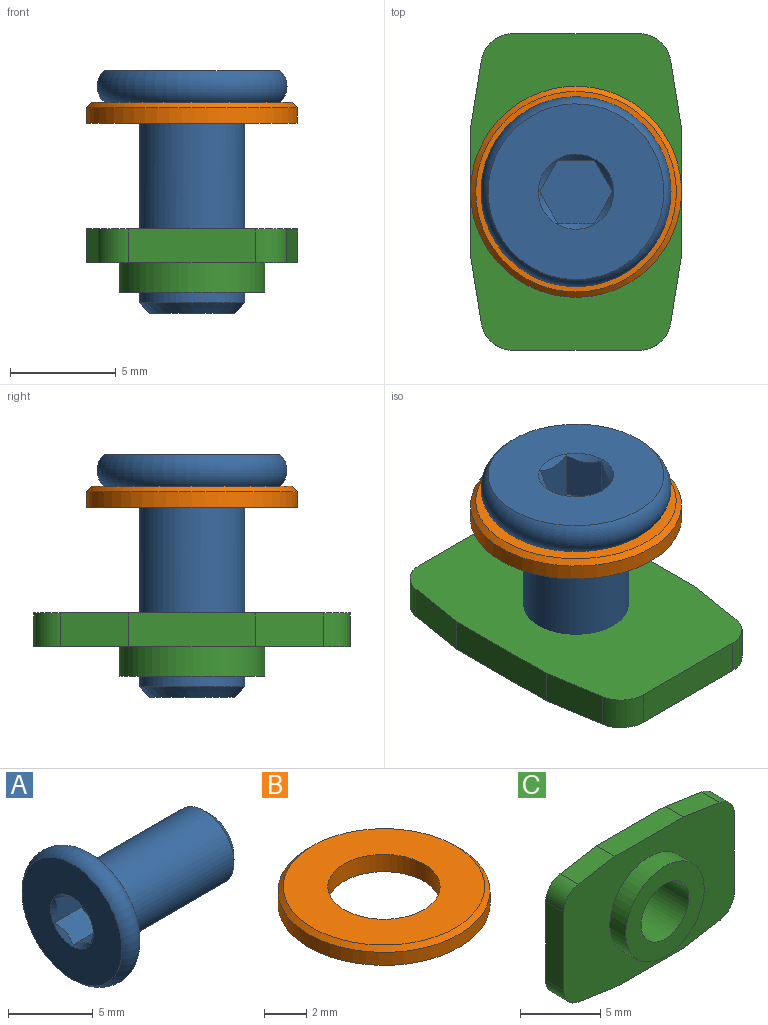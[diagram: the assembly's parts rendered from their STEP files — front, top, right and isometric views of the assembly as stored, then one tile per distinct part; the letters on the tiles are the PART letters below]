
ASSEMBLY  parts=3 mates=2
PART A: 14 faces, bbox 11.8x9.7x9.7 mm
  f0: cone r=1.78mm half-angle=45deg, axis (-1,0,0), area 3.1mm2, adj f5,f8,f9,f10,f11,f12,f13
  f1: torus R=3.5mm, axis (1,0,0), area 46.7mm2, adj f5,f6
  f2: cone r=2mm half-angle=45deg, axis (-1,0,0), area 10mm2, adj f3,f4
  f3: cylinder r=2.5mm len=9.5mm, axis (1,0,0), area 149.2mm2, adj f2,f6
  f4: plane 4x4mm, normal (1,0,0), area 12.6mm2, adj f2
  f5: plane 8.32x8.32mm, normal (-1,0,0), area 44.4mm2, adj f0,f1
  f6: plane 8.32x8.32mm, normal (1,0,0), area 34.8mm2, adj f1,f3
  f7: plane 3.46x3mm, normal (-1,0,0), area 7.8mm2, adj f8,f9,f10,f11,f12,f13
  f8: plane 2.25x1.5mm, normal (0,-0.5,-0.87), area 3.6mm2, adj f0,f7,f9,f13
  f9: plane 2.25x1.73mm, normal (0,-1,0), area 3.6mm2, adj f0,f7,f8,f10
  f10: plane 2.25x1.5mm, normal (0,-0.5,0.87), area 3.6mm2, adj f0,f7,f9,f11
  f11: plane 2.25x1.5mm, normal (0,0.5,0.87), area 3.6mm2, adj f0,f7,f10,f12
  f12: plane 2.25x1.73mm, normal (0,1,0), area 3.6mm2, adj f0,f7,f11,f13
  f13: plane 2.25x1.5mm, normal (0,0.5,-0.87), area 3.6mm2, adj f0,f7,f8,f12
PART B: 5 faces, bbox 10x10x1 mm
  f0: plane 9.5x9.5mm, normal (0,0,1), area 48.8mm2, adj f1,f4
  f1: cylinder r=2.65mm len=5.3mm, axis (0,0,-1), area 16.7mm2, adj f0,f2
  f2: plane 10x10mm, normal (0,0,-1), area 56.5mm2, adj f1,f3
  f3: cylinder r=5mm len=10mm, axis (0,0,-1), area 23.6mm2, adj f2,f4
  f4: cone r=5mm half-angle=45deg, axis (0,0,-1), area 10.8mm2, adj f0,f3
PART C: 17 faces, bbox 15x3x10 mm
  f0: cylinder r=2.1mm len=4.2mm, axis (0,-1,0), area 39.6mm2, adj f15,f16
  f1: cylinder r=3.45mm len=6.9mm, axis (0,1,0), area 30.3mm2, adj f2,f16
  f2: plane 15x10mm, normal (0,-1,0), area 104.8mm2, adj f1,f3,f4,f5,f6,f7,f8,f9
  f3: cylinder r=1.5mm len=1.6mm, axis (0,1,0), area 3.4mm2, adj f2,f4,f14,f15
  f4: plane 3.24x1.6mm, normal (0.16,0,0.99), area 5.2mm2, adj f2,f3,f5,f15
  f5: plane 6x1.6mm, normal (0,0,1), area 9.6mm2, adj f2,f4,f6,f15
  f6: plane 3.24x1.6mm, normal (-0.16,0,0.99), area 5.2mm2, adj f2,f5,f7,f15
  f7: cylinder r=1.5mm len=1.6mm, axis (0,1,0), area 3.4mm2, adj f2,f6,f8,f15
  f8: plane 6x1.6mm, normal (-1,0,0), area 9.6mm2, adj f2,f7,f9,f15
  f9: cylinder r=1.5mm len=1.6mm, axis (0,1,0), area 3.4mm2, adj f2,f8,f10,f15
  f10: plane 3.24x1.6mm, normal (-0.16,0,-0.99), area 5.2mm2, adj f2,f9,f11,f15
  f11: plane 6x1.6mm, normal (0,0,-1), area 9.6mm2, adj f2,f10,f12,f15
  f12: plane 3.24x1.6mm, normal (0.16,0,-0.99), area 5.2mm2, adj f2,f11,f13,f15
  f13: cylinder r=1.5mm len=1.6mm, axis (0,1,0), area 3.4mm2, adj f2,f12,f14,f15
  f14: plane 6x1.6mm, normal (1,0,0), area 9.6mm2, adj f2,f3,f13,f15
  f15: plane 15x10mm, normal (0,1,0), area 128.3mm2, adj f0,f3,f4,f5,f6,f7,f8,f9
  f16: plane 6.9x6.9mm, normal (0,-1,0), area 23.5mm2, adj f0,f1
PLACE A rot(axis=(0,1,0),90deg) t=(0,0,-7)mm
PLACE B t=(0,0,0.5)mm
PLACE C rot(axis=(0.58,0.58,0.58),120deg) t=(0,0,-5)mm
MATE fastened C.f0 <-> B.f1  axis (0,0,1) through (0,0,-5)mm
MATE fastened A.f0 <-> B.f1  axis (0,0,-1) through (0,0,1)mm
